# Revit family: Runoff_Leg-Teknion-CROL-Chronicle-Overlap_To_Credenza-R2022
name_source: partatom
category: Furniture
units: mm (PartAtom-declared; Revit-internal decimal feet)

## family parameters
Always vertical = Yes
Cut with Voids When Loaded = No
OmniClass Number = 23.40.20.00
OmniClass Title = General Furniture and Specialties
Render Appearance Source = Family Geometry
Room Calculation Point = No
Shared = Yes
Work Plane-Based = No

## types (5) — shared parameters
Assembly Code = E2020200
Description = Chronicle Runoff, Leg, Overlap to Credenza
Height = 29 "
Manufacturer = Teknion
Manufacturer Fax = 416.661.4586
Part Number = CROL
Product Page URL = https://www.teknion.com
Series = Chronicle
Sustainability Data = https://www.teknion.com
URL = www.teknion.com
Unit Weight URL = http://www.teknion.com
Warranty = http://www.teknion.com
zero-valued in all types: Default Elevation, Length

## per-type parameters (varying)
| type | Model | Width |
| 60" Width | CROL__60___ | 60 " |
| 66" Width | CROL__66___ | 66 " |
| 72" Width | CROL__72___ | 72 " |
| 78" Width | CROL__78___ | 78 " |
| 84" Width | CROL__84___ | 84 " |

## geometry (parser evidence)
native form markers: Sweep x8
no freeform markers — native parametric forms only
